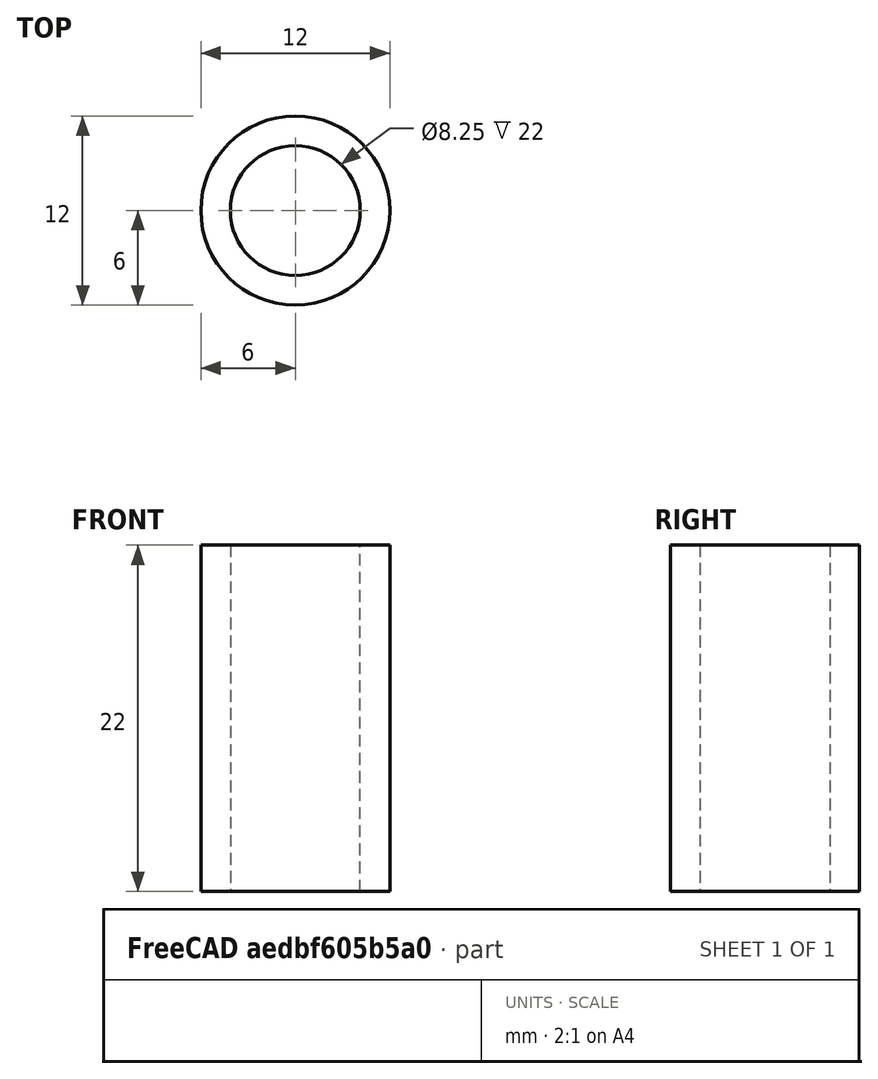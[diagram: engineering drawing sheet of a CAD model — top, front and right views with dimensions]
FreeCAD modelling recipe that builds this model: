
FCSTD DOCUMENT  (FreeCAD 0.20R27319 (Git))
Label: Filament Holder Centre
License: All rights reserved
LicenseURL: http://en.wikipedia.org/wiki/All_rights_reserved
objects: Sketcher::SketchObject×1, PartDesign::Pad×1, PartDesign::Body×1
note: 4 computed .brp shape members not serialized (recipe doc carries the construction recipe); baked Part::Feature solids carry a one-line shape summary decoded from their .brp

FEATURE [Sketcher::SketchObject] Sketch001
  FullyConstrained = false
  MapMode = 5
  Placement = pos=(0,0,3) rot=(0,0,1;0rad)
  sketch-geometry (3):
    g0: Circle CenterX=0 CenterY=0 CenterZ=0 NormalX=0 NormalY=0 NormalZ=1 AngleXU=0 Radius=4.125
    g1: Circle CenterX=0 CenterY=0 CenterZ=0 NormalX=0 NormalY=0 NormalZ=1 AngleXU=0 Radius=6
    g2: GeomPoint X=0 Y=0 Z=0
  constraints (4):
    c: Coincident(g0,g-1)
    c: Coincident(g1,g0)
    c: Diameter(g0) = 8.25
    c: Diameter(g1) = 12
FEATURE [PartDesign::Pad] Pad001
  Direction = (0,0,1)
  Length = 22
  Length2 = 10
  Placement = pos=(0,0,3) rot=(0,0,1;0rad)
  Profile = -> Sketch001
  ReferenceAxis = -> Sketch001 [N_Axis]
  Type = 0
FEATURE [PartDesign::Body] Body
  Group = -> [Sketch001,Pad001]
  Origin = -> Origin
  Tip = -> Pad001
